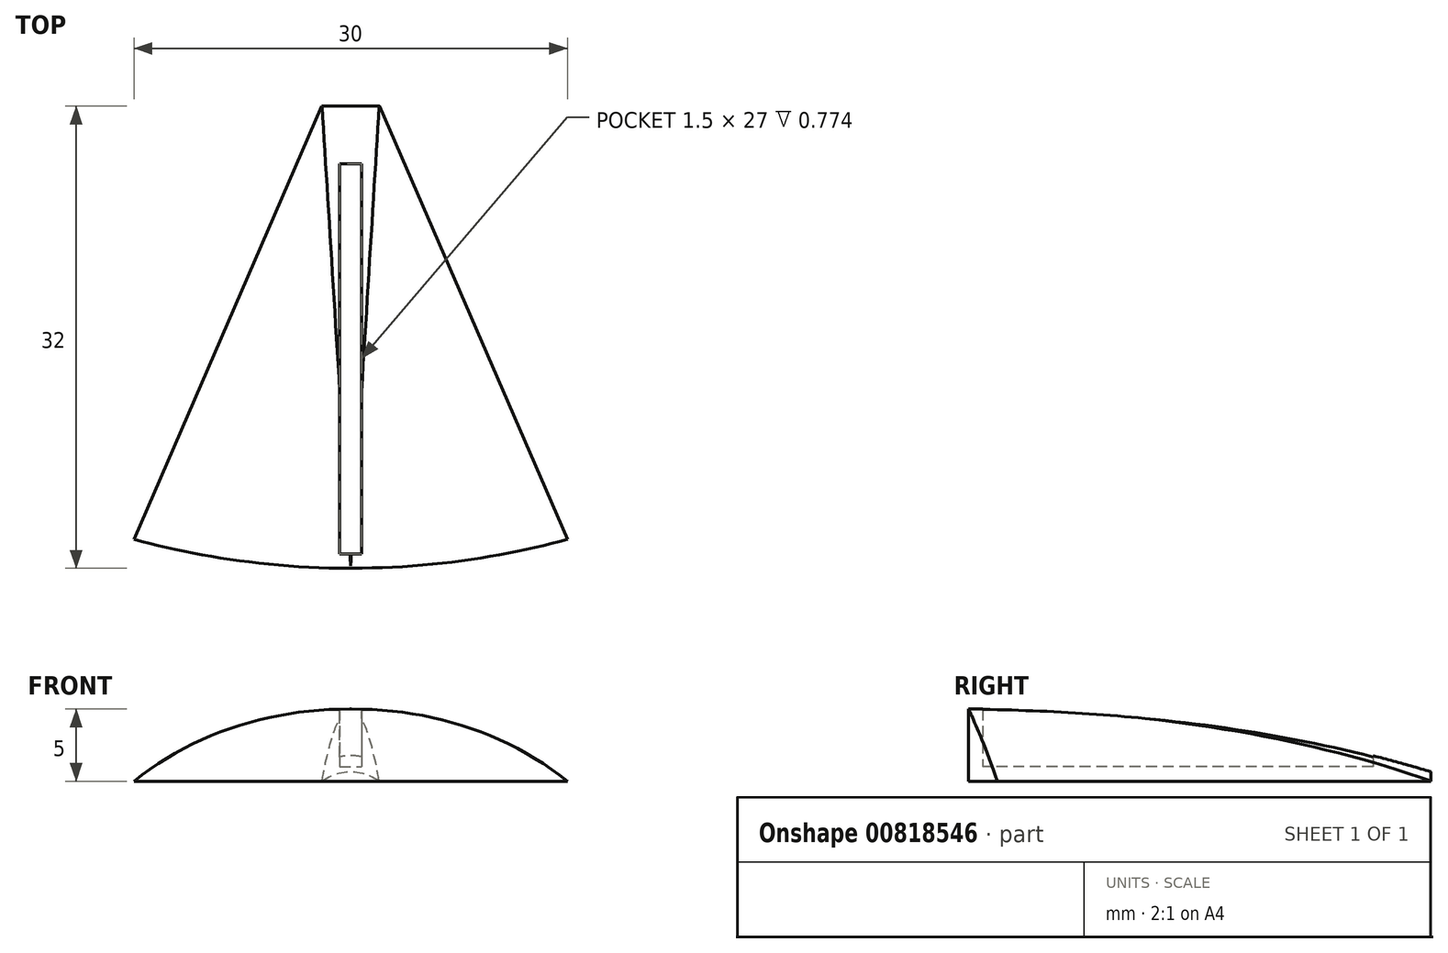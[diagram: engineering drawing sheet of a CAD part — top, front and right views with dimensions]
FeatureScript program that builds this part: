
annotation { "Feature Type Name" : "Feature", "Feature Type Description" : "" }
export const myFeature = defineFeature(function(context is Context, id is Id, definition is map)
    precondition{}
    {
        {
            var Q0;
            Q0=qCreatedBy(makeId("Top.planeOp"),FACE);
            var sketch = newSketch(context, id + "F0", { "sketchPlane" : qUnion([Q0])});
            skLineSegment(sketch, "E0", {"start": v(0, -15.98) * mm, "end": v(15, -15.98) * mm});
            skLineSegment(sketch, "E1", {"start": v(15, -15.98) * mm, "end": v(-15, -15.98) * mm});
            skLineSegment(sketch, "E2", {"start": v(0, -15.98) * mm, "end": v(0, 14.02) * mm});
            skLineSegment(sketch, "E3", {"start": v(0, 14.02) * mm, "end": v(2, 14.02) * mm});
            skLineSegment(sketch, "E4", {"start": v(0, 14.02) * mm, "end": v(-2, 14.02) * mm});
            skLineSegment(sketch, "E5", {"start": v(-2, 14.02) * mm, "end": v(-15, -15.98) * mm});
            skLineSegment(sketch, "E6", {"start": v(15, -15.98) * mm, "end": v(2, 14.02) * mm});
            skArc(sketch, "E7", {"start": v(-15, -15.98) * mm, "mid": v(0, -17.98) * mm, "end": v(15, -15.98) * mm});
            skPoint(sketch, "E8", {"position": v(0, -17.98) * mm});
            skLineSegment(sketch, "E9", {"start": v(0, 0) * mm, "end": v(-0.75, 0) * mm});
            skLineSegment(sketch, "E10", {"start": v(-0.75, 0) * mm, "end": v(0.75, 0) * mm});
            skLineSegment(sketch, "E11", {"start": v(0.75, 0) * mm, "end": v(0.75, -17.97) * mm});
            skLineSegment(sketch, "E12", {"start": v(-0.75, 0) * mm, "end": v(-0.75, -17.97) * mm});
            skLineSegment(sketch, "E13", {"start": v(-0.75, 0) * mm, "end": v(-0.75, 10.02) * mm});
            skLineSegment(sketch, "E14", {"start": v(-0.75, 10.02) * mm, "end": v(0.75, 10.02) * mm});
            skLineSegment(sketch, "E15", {"start": v(0.75, 10.02) * mm, "end": v(0.75, 0) * mm});
            skLineSegment(sketch, "E16", {"start": v(-0.75, -16.98) * mm, "end": v(0.75, -16.98) * mm});
            skSolve(sketch);
        }
        {
            var Q0;
            {var subQ1=sQuery(id+"F0.wireOp",EDGE,"E4");Q0=makeQuery(id+"F0.imprint","IMPRINT",FACE,{"disambiguationData":[TD([[makeQuery(id+"F0.imprint","IMPRINT",EDGE,{"derivedFrom":subQ1}),1.0]])]});}
            var Q1;
            {var subQ0=sQuery(id+"F0.wireOp",EDGE,"E3");Q1=makeQuery(id+"F0.imprint","IMPRINT",FACE,{"disambiguationData":[TD([[makeQuery(id+"F0.imprint","IMPRINT",EDGE,{"derivedFrom":subQ0}),-1.0]])]});}
            var Q2;
            {var subQ0=sQuery(id+"F0.wireOp",EDGE,"E11");var subQ1=sQuery(id+"F0.wireOp",EDGE,"E0");var subQ2=makeQuery(id+"F0.imprint","INTERSECT",VERTEX,{"derivedFrom":[subQ1,subQ0]});Q2=makeQuery(id+"F0.imprint","IMPRINT",FACE,{"disambiguationData":[TD([[makeQuery(id+"F0.imprint","IMPRINT",EDGE,{"disambiguationData":[TD([[subQ2,-1.0]])],"derivedFrom":subQ0}),1.0]])]});}
            var Q3;
            {var subQ0=sQuery(id+"F0.wireOp",EDGE,"E12");var subQ1=sQuery(id+"F0.wireOp",EDGE,"E1");var subQ2=makeQuery(id+"F0.imprint","INTERSECT",VERTEX,{"derivedFrom":[subQ1,subQ0]});Q3=makeQuery(id+"F0.imprint","IMPRINT",FACE,{"disambiguationData":[TD([[makeQuery(id+"F0.imprint","IMPRINT",EDGE,{"disambiguationData":[TD([[subQ2,-1.0]])],"derivedFrom":subQ0}),-1.0]])]});}
            var Q4;
            {var subQ5=sQuery(id+"F0.wireOp",EDGE,"E16");Q4=makeQuery(id+"F0.imprint","IMPRINT",FACE,{"disambiguationData":[TD([[makeQuery(id+"F0.imprint","IMPRINT",EDGE,{"derivedFrom":subQ5}),-1.0]])]});}
            extrude(context, id + "F1", {"entities" : qUnion([Q0, Q1, Q2, Q3, Q4]), "depth" : 5 * mm, "offsetDistance" : 25 * mm});
        }
        {
            var Q0;
            Q0=makeQuery(id+"F1.opExtrude","CAP_EDGE",EDGE,{"disambiguationData":[OSD([sQuery(id+"F0.wireOp",EDGE,"E5")])],"isStart":false});
            var Q1;
            Q1=makeQuery(id+"F1.opExtrude","CAP_EDGE",EDGE,{"disambiguationData":[OSD([sQuery(id+"F0.wireOp",EDGE,"E6")])],"isStart":false});
            fillet(context, id + "F2", {"entities" : qUnion([Q0, Q1]), "radius" : 23.5 * mm, "tangentPropagation" : true, "allowEdgeOverflow" : false});
        }
        {
            var Q0;
            {var subQ3=sQuery(id+"F0.wireOp",EDGE,"E16");Q0=makeQuery(id+"F0.imprint","IMPRINT",FACE,{"disambiguationData":[TD([[makeQuery(id+"F0.imprint","IMPRINT",EDGE,{"derivedFrom":subQ3}),1.0]])]});}
            var Q1;
            {var subQ0=sQuery(id+"F0.wireOp",EDGE,"E9");Q1=makeQuery(id+"F0.imprint","IMPRINT",FACE,{"disambiguationData":[TD([[makeQuery(id+"F0.imprint","IMPRINT",EDGE,{"derivedFrom":subQ0}),-1.0]])]});}
            var Q2;
            {var subQ0=sQuery(id+"F0.wireOp",EDGE,"E10");Q2=makeQuery(id+"F0.imprint","IMPRINT",FACE,{"disambiguationData":[TD([[makeQuery(id+"F0.imprint","IMPRINT",EDGE,{"derivedFrom":subQ0}),1.0]])]});}
            var Q3;
            {var subQ5=sQuery(id+"F0.wireOp",EDGE,"E10");Q3=makeQuery(id+"F0.imprint","IMPRINT",FACE,{"disambiguationData":[TD([[makeQuery(id+"F0.imprint","IMPRINT",EDGE,{"derivedFrom":subQ5}),-1.0]])]});}
            var Q4;
            {var subQ5=sQuery(id+"F0.wireOp",EDGE,"E9");Q4=makeQuery(id+"F0.imprint","IMPRINT",FACE,{"disambiguationData":[TD([[makeQuery(id+"F0.imprint","IMPRINT",EDGE,{"derivedFrom":subQ5}),1.0]])]});}
            extrude(context, id + "F3", {"entities" : qUnion([Q0, Q1, Q2, Q3, Q4]), "operationType" : NewBodyOperationType.ADD, "depth" : 1 * mm, "offsetDistance" : 25 * mm});
        }
        {
            var Q0;
            {var subQ0=makeQuery(id+"F1.opExtrude","CAP_EDGE",EDGE,{"disambiguationData":[OSD([sQuery(id+"F0.wireOp",EDGE,"E6")])],"isStart":false});var subQ1=makeQuery(id+"F1.opExtrude","CAP_EDGE",EDGE,{"disambiguationData":[OSD([sQuery(id+"F0.wireOp",EDGE,"E5")])],"isStart":false});Q0=qUnion([makeQuery(id+"F2.opFillet","BLEND_EDGE",EDGE,{"disambiguationData":[OD(1.0)],"blendedFrom":[subQ1,subQ0],"blendedInto":[]}),makeQuery(id+"F2.opFillet","BLEND_EDGE",EDGE,{"disambiguationData":[OD(0.0)],"blendedFrom":[subQ1,subQ0],"blendedInto":[]})]);}
            fillet(context, id + "F4", {"entities" : qUnion([Q0]), "radius" : 3.5 * mm, "tangentPropagation" : true, "allowEdgeOverflow" : false});
        }
    });
